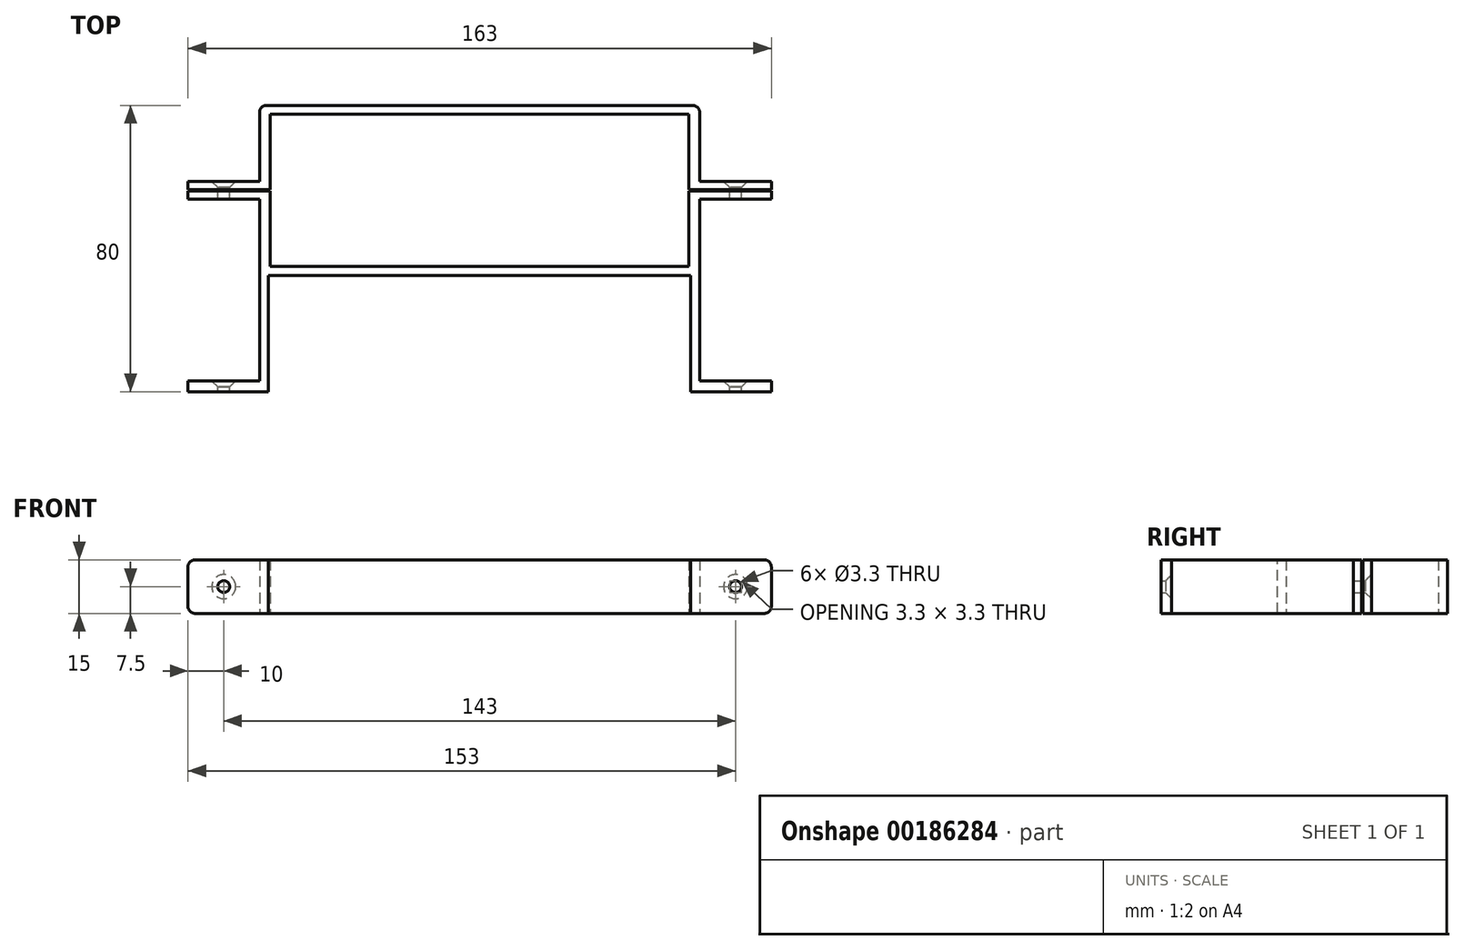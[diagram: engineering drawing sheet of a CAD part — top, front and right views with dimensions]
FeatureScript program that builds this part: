
annotation { "Feature Type Name" : "Feature", "Feature Type Description" : "" }
export const myFeature = defineFeature(function(context is Context, id is Id, definition is map)
    precondition{}
    {
        {
            var Q0;
            Q0=qCreatedBy(makeId("Top.planeOp"),FACE);
            var sketch = newSketch(context, id + "F0", { "sketchPlane" : qUnion([Q0])});
            skLineSegment(sketch, "E0.bottom", {"start": v(61.5, -23.75) * mm, "end": v(-61.5, -23.75) * mm});
            skLineSegment(sketch, "E0.top", {"start": v(61.5, 23.75) * mm, "end": v(-61.5, 23.75) * mm});
            skLineSegment(sketch, "E0.left", {"start": v(61.5, -23.75) * mm, "end": v(61.5, 23.75) * mm});
            skLineSegment(sketch, "E0.right", {"start": v(-61.5, -23.75) * mm, "end": v(-61.5, 23.75) * mm});
            skPoint(sketch, "E0.middle", {"position": v(0, 0) * mm});
            skLineSegment(sketch, "E1.bottom", {"start": v(58.5, -21.25) * mm, "end": v(-58.5, -21.25) * mm});
            skLineSegment(sketch, "E1.top", {"start": v(58.5, 21.25) * mm, "end": v(-58.5, 21.25) * mm});
            skLineSegment(sketch, "E1.left", {"start": v(58.5, -21.25) * mm, "end": v(58.5, 21.25) * mm});
            skLineSegment(sketch, "E1.right", {"start": v(-58.5, -21.25) * mm, "end": v(-58.5, 21.25) * mm});
            skSolve(sketch);
        }
        {
            var Q0;
            Q0=makeQuery(id+"F0.imprint","IMPRINT",FACE,{"disambiguationData":[TD([[makeQuery(id+"F0.imprint","IMPRINT",EDGE,{"derivedFrom":sQuery(id+"F0.wireOp",EDGE,"E0.bottom")}),-1.0]])]});
            extrude(context, id + "F1", {"entities" : qUnion([Q0]), "depth" : 15 * mm, "offsetDistance" : 25 * mm});
        }
        {
            var Q0;
            Q0=makeQuery(id+"F1.opExtrude","CAP_FACE",FACE,{"disambiguationData":[OSD([sQuery(id+"F0.wireOp",EDGE,"E0.bottom"),sQuery(id+"F0.wireOp",EDGE,"E0.top"),sQuery(id+"F0.wireOp",EDGE,"E0.left"),sQuery(id+"F0.wireOp",EDGE,"E0.right"),sQuery(id+"F0.wireOp",EDGE,"E1.bottom"),sQuery(id+"F0.wireOp",EDGE,"E1.top"),sQuery(id+"F0.wireOp",EDGE,"E1.left"),sQuery(id+"F0.wireOp",EDGE,"E1.right")])],"isStart":false});
            var sketch = newSketch(context, id + "F2", { "sketchPlane" : qUnion([Q0])});
            skLineSegment(sketch, "E2.bottom", {"start": v(-55, -25) * mm, "end": v(55, -25) * mm});
            skLineSegment(sketch, "E2.top", {"start": v(-55, 25) * mm, "end": v(55, 25) * mm});
            skLineSegment(sketch, "E2.left", {"start": v(-55, -25) * mm, "end": v(-55, 25) * mm});
            skLineSegment(sketch, "E2.right", {"start": v(55, -25) * mm, "end": v(55, 25) * mm});
            skPoint(sketch, "E2.middle", {"position": v(0, 0) * mm});
            skSolve(sketch);
        }
        {
            var Q0;
            Q0=makeQuery(id+"F1.opExtrude","SWEPT_FACE",FACE,{"disambiguationData":[OSD([sQuery(id+"F0.wireOp",EDGE,"E0.bottom")])]});
            var sketch = newSketch(context, id + "F3", { "sketchPlane" : qUnion([Q0])});
            skPoint(sketch, "E3", {"position": v(-59, 15) * mm});
            skPoint(sketch, "E4", {"position": v(-59, 0) * mm});
            skPoint(sketch, "E5", {"position": v(59, 15) * mm});
            skPoint(sketch, "E6", {"position": v(59, 0) * mm});
            skLineSegment(sketch, "E7", {"start": v(-59, 15) * mm, "end": v(-59, 0) * mm});
            skLineSegment(sketch, "E8", {"start": v(59, 0) * mm, "end": v(59, 15) * mm});
            skSolve(sketch);
        }
        {
            var Q0;
            {var subQ0=sQuery(id+"F3.wireOp",EDGE,"E7");Q0=makeQuery(id+"F3.imprint","IMPRINT",FACE,{"disambiguationData":[TD([[makeQuery(id+"F3.imprint","IMPRINT",EDGE,{"derivedFrom":subQ0}),-1.0]])]});}
            var Q1;
            {var subQ0=sQuery(id+"F3.wireOp",EDGE,"E8");Q1=makeQuery(id+"F3.imprint","IMPRINT",FACE,{"disambiguationData":[TD([[makeQuery(id+"F3.imprint","IMPRINT",EDGE,{"derivedFrom":subQ0}),-1.0]])]});}
            extrude(context, id + "F4", {"entities" : qUnion([Q0, Q1]), "operationType" : NewBodyOperationType.ADD, "depth" : 32.5 * mm, "offsetDistance" : 25 * mm});
        }
        {
            var Q0;
            {var subQ0=sQuery(id+"F0.wireOp",EDGE,"E0.right");Q0=makeQuery(id+"F4.boolean.opBoolean","MERGE",FACE,{"derivedFrom":[makeQuery(id+"F1.opExtrude","SWEPT_FACE",FACE,{"disambiguationData":[OSD([subQ0])]}),makeQuery(id+"F4.opExtrude","SWEPT_FACE",FACE,{"disambiguationData":[OSD([sQuery(id+"F0.wireOp",EDGE,"E0.bottom"),subQ0])]})]});}
            var sketch = newSketch(context, id + "F5", { "sketchPlane" : qUnion([Q0])});
            skPoint(sketch, "E9", {"position": v(53.25, 15) * mm});
            skPoint(sketch, "E10", {"position": v(53.25, 0) * mm});
            skLineSegment(sketch, "E11", {"start": v(53.25, 15) * mm, "end": v(53.25, 0) * mm});
            skSolve(sketch);
        }
        {
            var Q0;
            {var subQ0=sQuery(id+"F5.wireOp",EDGE,"E11");Q0=makeQuery(id+"F5.imprint","IMPRINT",FACE,{"disambiguationData":[TD([[makeQuery(id+"F5.imprint","IMPRINT",EDGE,{"derivedFrom":subQ0}),1.0]])]});}
            extrude(context, id + "F6", {"entities" : qUnion([Q0]), "operationType" : NewBodyOperationType.ADD, "depth" : 20 * mm, "offsetDistance" : 25 * mm});
        }
        {
            var Q0;
            {var subQ0=sQuery(id+"F0.wireOp",EDGE,"E0.left");Q0=makeQuery(id+"F4.boolean.opBoolean","MERGE",FACE,{"derivedFrom":[makeQuery(id+"F1.opExtrude","SWEPT_FACE",FACE,{"disambiguationData":[OSD([subQ0])]}),makeQuery(id+"F4.opExtrude","SWEPT_FACE",FACE,{"disambiguationData":[OSD([sQuery(id+"F0.wireOp",EDGE,"E0.bottom"),subQ0])]})]});}
            var sketch = newSketch(context, id + "F7", { "sketchPlane" : qUnion([Q0])});
            skPoint(sketch, "E12", {"position": v(-53.25, 15) * mm});
            skPoint(sketch, "E13", {"position": v(-53.25, 0) * mm});
            skLineSegment(sketch, "E14", {"start": v(-53.25, 15) * mm, "end": v(-53.25, 0) * mm});
            skSolve(sketch);
        }
        {
            var Q0;
            {var subQ0=sQuery(id+"F7.wireOp",EDGE,"E14");Q0=makeQuery(id+"F7.imprint","IMPRINT",FACE,{"disambiguationData":[TD([[makeQuery(id+"F7.imprint","IMPRINT",EDGE,{"derivedFrom":subQ0}),-1.0]])]});}
            extrude(context, id + "F8", {"entities" : qUnion([Q0]), "operationType" : NewBodyOperationType.ADD, "depth" : 20 * mm, "offsetDistance" : 25 * mm});
        }
        {
            var Q0;
            Q0=makeQuery(id+"F8.opExtrude","SWEPT_FACE",FACE,{"disambiguationData":[OSD([sQuery(id+"F7.wireOp",EDGE,"E14")])]});
            var sketch = newSketch(context, id + "F9", { "sketchPlane" : qUnion([Q0])});
            skPoint(sketch, "E15", {"position": v(-71.5, 7.5) * mm});
            skPoint(sketch, "E15.positionSnap0", {"position": v(-71.5, 0) * mm});
            skPoint(sketch, "E15.positionSnap1", {"position": v(-61.5, 7.5) * mm});
            skSolve(sketch);
        }
        {
            var Q0;
            Q0=sQuery(id+"F9.wireOp",VERTEX,"E15");
            var Q1;
            Q1=makeQuery(id+"F1.opExtrude","SWEPT_BODY",BODY,{"disambiguationData":[OSD([sQuery(id+"F0.wireOp",EDGE,"E0.bottom"),sQuery(id+"F0.wireOp",EDGE,"E0.top"),sQuery(id+"F0.wireOp",EDGE,"E0.left"),sQuery(id+"F0.wireOp",EDGE,"E0.right"),sQuery(id+"F0.wireOp",EDGE,"E1.bottom"),sQuery(id+"F0.wireOp",EDGE,"E1.top"),sQuery(id+"F0.wireOp",EDGE,"E1.left"),sQuery(id+"F0.wireOp",EDGE,"E1.right")])]});
            hole(context, id + "F10", {"style" : HoleStyle.C_SINK, "endStyle" : HoleEndStyle.BLIND, "standardTappedOrClearance" : lookupTablePath({ "standard" : "ISO", "fit" : "Normal", "size" : "M3", "type" : "Clearance" }), "standardBlindInLast" : lookupTablePath({ "fit" : "Standard", "standard" : "ISO", "size" : "M3", "type" : "Clearance" }), "holeDiameter" : 3.3 * mm, "cSinkDiameter" : 6.72 * mm, "cSinkAngle" : 90 * degree, "majorDiameter" : 5 * mm, "holeDepth" : 5 * mm, "isTappedThrough" : true, "tappedDepth" : 12 * mm, "tapClearance" : 3, "startFromSketch" : true, "locations" : qUnion([Q0]), "scope" : qUnion([Q1])});
        }
        {
            var Q0;
            Q0=makeQuery(id+"F6.opExtrude","SWEPT_FACE",FACE,{"disambiguationData":[OSD([sQuery(id+"F5.wireOp",EDGE,"E11")])]});
            var sketch = newSketch(context, id + "F11", { "sketchPlane" : qUnion([Q0])});
            skPoint(sketch, "E16", {"position": v(71.5, 7.5) * mm});
            skPoint(sketch, "E16.positionSnap0", {"position": v(81.5, 7.5) * mm});
            skPoint(sketch, "E16.positionSnap1", {"position": v(71.5, 0) * mm});
            skSolve(sketch);
        }
        {
            var Q0;
            Q0=sQuery(id+"F11.wireOp",VERTEX,"E16");
            var Q1;
            Q1=makeQuery(id+"F1.opExtrude","SWEPT_BODY",BODY,{"disambiguationData":[OSD([sQuery(id+"F0.wireOp",EDGE,"E0.bottom"),sQuery(id+"F0.wireOp",EDGE,"E0.top"),sQuery(id+"F0.wireOp",EDGE,"E0.left"),sQuery(id+"F0.wireOp",EDGE,"E0.right"),sQuery(id+"F0.wireOp",EDGE,"E1.bottom"),sQuery(id+"F0.wireOp",EDGE,"E1.top"),sQuery(id+"F0.wireOp",EDGE,"E1.left"),sQuery(id+"F0.wireOp",EDGE,"E1.right")])]});
            hole(context, id + "F12", {"style" : HoleStyle.C_SINK, "endStyle" : HoleEndStyle.BLIND, "standardTappedOrClearance" : lookupTablePath({ "standard" : "ISO", "fit" : "Normal", "size" : "M3", "type" : "Clearance" }), "standardBlindInLast" : lookupTablePath({ "fit" : "Standard", "standard" : "ISO", "size" : "M3", "type" : "Clearance" }), "holeDiameter" : 3.3 * mm, "cSinkDiameter" : 6.72 * mm, "cSinkAngle" : 90 * degree, "majorDiameter" : 5 * mm, "holeDepth" : 5 * mm, "isTappedThrough" : true, "tappedDepth" : 12 * mm, "tapClearance" : 3, "startFromSketch" : true, "locations" : qUnion([Q0]), "scope" : qUnion([Q1])});
        }
        {
            var Q0;
            {var subQ0=sQuery(id+"F0.wireOp",EDGE,"E0.right");Q0=makeQuery(id+"F4.boolean.opBoolean","MERGE",FACE,{"derivedFrom":[makeQuery(id+"F1.opExtrude","SWEPT_FACE",FACE,{"disambiguationData":[OSD([subQ0])]}),makeQuery(id+"F4.opExtrude","SWEPT_FACE",FACE,{"disambiguationData":[OSD([sQuery(id+"F0.wireOp",EDGE,"E0.bottom"),subQ0])]})]});}
            var sketch = newSketch(context, id + "F13", { "sketchPlane" : qUnion([Q0])});
            skPoint(sketch, "E17", {"position": v(-2.5, 0) * mm});
            skPoint(sketch, "E18", {"position": v(2.5, 0) * mm});
            skPoint(sketch, "E19", {"position": v(2.5, 15) * mm});
            skPoint(sketch, "E20", {"position": v(-2.5, 15) * mm});
            skPoint(sketch, "E21", {"position": v(0, 0) * mm});
            skPoint(sketch, "E22", {"position": v(0, 15) * mm});
            skLineSegment(sketch, "E23", {"start": v(-2.5, 0) * mm, "end": v(-2.5, 15) * mm});
            skLineSegment(sketch, "E24", {"start": v(2.5, 15) * mm, "end": v(2.5, 0) * mm});
            skSolve(sketch);
        }
        {
            var Q0;
            {var subQ0=sQuery(id+"F13.wireOp",EDGE,"E23");Q0=makeQuery(id+"F13.imprint","IMPRINT",FACE,{"disambiguationData":[TD([[makeQuery(id+"F13.imprint","IMPRINT",EDGE,{"derivedFrom":subQ0}),-1.0]])]});}
            extrude(context, id + "F14", {"entities" : qUnion([Q0]), "operationType" : NewBodyOperationType.ADD, "depth" : 20 * mm, "offsetDistance" : 25 * mm});
        }
        {
            var Q0;
            Q0=makeQuery(id+"F14.opExtrude","SWEPT_FACE",FACE,{"disambiguationData":[OSD([sQuery(id+"F13.wireOp",EDGE,"E23")])]});
            var sketch = newSketch(context, id + "F15", { "sketchPlane" : qUnion([Q0])});
            skPoint(sketch, "E25", {"position": v(71.5, 7.5) * mm});
            skPoint(sketch, "E25.positionSnap0", {"position": v(71.5, 0) * mm});
            skPoint(sketch, "E25.positionSnap1", {"position": v(81.5, 7.5) * mm});
            skSolve(sketch);
        }
        {
            var Q0;
            Q0=sQuery(id+"F15.wireOp",VERTEX,"E25");
            var Q1;
            Q1=makeQuery(id+"F1.opExtrude","SWEPT_BODY",BODY,{"disambiguationData":[OSD([sQuery(id+"F0.wireOp",EDGE,"E0.bottom"),sQuery(id+"F0.wireOp",EDGE,"E0.top"),sQuery(id+"F0.wireOp",EDGE,"E0.left"),sQuery(id+"F0.wireOp",EDGE,"E0.right"),sQuery(id+"F0.wireOp",EDGE,"E1.bottom"),sQuery(id+"F0.wireOp",EDGE,"E1.top"),sQuery(id+"F0.wireOp",EDGE,"E1.left"),sQuery(id+"F0.wireOp",EDGE,"E1.right")])]});
            hole(context, id + "F16", {"style" : HoleStyle.C_SINK, "endStyle" : HoleEndStyle.THROUGH, "standardTappedOrClearance" : lookupTablePath({ "standard" : "ISO", "fit" : "Normal", "size" : "M3", "type" : "Clearance" }), "standardBlindInLast" : lookupTablePath({ "fit" : "Standard", "standard" : "ISO", "size" : "M3", "type" : "Clearance" }), "holeDiameter" : 3.3 * mm, "cSinkDiameter" : 6.72 * mm, "cSinkAngle" : 90 * degree, "majorDiameter" : 5 * mm, "isTappedThrough" : true, "tappedDepth" : 12 * mm, "tapClearance" : 3, "startFromSketch" : true, "locations" : qUnion([Q0]), "scope" : qUnion([Q1])});
        }
        {
            var Q0;
            {var subQ0=sQuery(id+"F0.wireOp",EDGE,"E0.left");Q0=makeQuery(id+"F4.boolean.opBoolean","MERGE",FACE,{"derivedFrom":[makeQuery(id+"F1.opExtrude","SWEPT_FACE",FACE,{"disambiguationData":[OSD([subQ0])]}),makeQuery(id+"F4.opExtrude","SWEPT_FACE",FACE,{"disambiguationData":[OSD([sQuery(id+"F0.wireOp",EDGE,"E0.bottom"),subQ0])]})]});}
            var sketch = newSketch(context, id + "F17", { "sketchPlane" : qUnion([Q0])});
            skPoint(sketch, "E26", {"position": v(0, 0) * mm});
            skPoint(sketch, "E27", {"position": v(0, 15) * mm});
            skPoint(sketch, "E28", {"position": v(2.5, 15) * mm});
            skPoint(sketch, "E29", {"position": v(2.5, 0) * mm});
            skPoint(sketch, "E30", {"position": v(-2.5, 0) * mm});
            skPoint(sketch, "E31", {"position": v(-2.5, 15) * mm});
            skLineSegment(sketch, "E32", {"start": v(-2.5, 15) * mm, "end": v(-2.5, 0) * mm});
            skLineSegment(sketch, "E33", {"start": v(2.5, 0) * mm, "end": v(2.5, 15) * mm});
            skSolve(sketch);
        }
        {
            var Q0;
            {var subQ0=sQuery(id+"F17.wireOp",EDGE,"E32");Q0=makeQuery(id+"F17.imprint","IMPRINT",FACE,{"disambiguationData":[TD([[makeQuery(id+"F17.imprint","IMPRINT",EDGE,{"derivedFrom":subQ0}),1.0]])]});}
            extrude(context, id + "F18", {"entities" : qUnion([Q0]), "operationType" : NewBodyOperationType.ADD, "depth" : 20 * mm, "offsetDistance" : 25 * mm});
        }
        {
            var Q0;
            Q0=makeQuery(id+"F18.opExtrude","SWEPT_FACE",FACE,{"disambiguationData":[OSD([sQuery(id+"F17.wireOp",EDGE,"E33")])]});
            var sketch = newSketch(context, id + "F19", { "sketchPlane" : qUnion([Q0])});
            skPoint(sketch, "E34", {"position": v(-71.5, 7.5) * mm});
            skPoint(sketch, "E34.positionSnap0", {"position": v(-71.5, 15) * mm});
            skPoint(sketch, "E34.positionSnap1", {"position": v(-81.5, 7.5) * mm});
            skSolve(sketch);
        }
        {
            var Q0;
            Q0=sQuery(id+"F19.wireOp",VERTEX,"E34");
            var Q1;
            Q1=makeQuery(id+"F1.opExtrude","SWEPT_BODY",BODY,{"disambiguationData":[OSD([sQuery(id+"F0.wireOp",EDGE,"E0.bottom"),sQuery(id+"F0.wireOp",EDGE,"E0.top"),sQuery(id+"F0.wireOp",EDGE,"E0.left"),sQuery(id+"F0.wireOp",EDGE,"E0.right"),sQuery(id+"F0.wireOp",EDGE,"E1.bottom"),sQuery(id+"F0.wireOp",EDGE,"E1.top"),sQuery(id+"F0.wireOp",EDGE,"E1.left"),sQuery(id+"F0.wireOp",EDGE,"E1.right")])]});
            hole(context, id + "F20", {"style" : HoleStyle.C_SINK, "endStyle" : HoleEndStyle.THROUGH, "standardTappedOrClearance" : lookupTablePath({ "standard" : "ISO", "fit" : "Normal", "size" : "M3", "type" : "Clearance" }), "standardBlindInLast" : lookupTablePath({ "fit" : "Standard", "standard" : "ISO", "size" : "M3", "type" : "Clearance" }), "holeDiameter" : 3.3 * mm, "cSinkDiameter" : 6.72 * mm, "cSinkAngle" : 90 * degree, "majorDiameter" : 5 * mm, "isTappedThrough" : true, "tappedDepth" : 12 * mm, "tapClearance" : 3, "startFromSketch" : true, "locations" : qUnion([Q0]), "scope" : qUnion([Q1])});
        }
        {
            var Q0;
            Q0=makeQuery(id+"F18.opExtrude","CAP_FACE",FACE,{"disambiguationData":[OSD([sQuery(id+"F0.wireOp",EDGE,"E0.bottom"),sQuery(id+"F0.wireOp",EDGE,"E0.left"),sQuery(id+"F17.wireOp",EDGE,"E32"),sQuery(id+"F17.wireOp",EDGE,"E33")])],"isStart":false});
            var sketch = newSketch(context, id + "F21", { "sketchPlane" : qUnion([Q0])});
            skPoint(sketch, "E35", {"position": v(0, 0) * mm});
            skPoint(sketch, "E36", {"position": v(0, 15) * mm});
            skPoint(sketch, "E37", {"position": v(0.2, 15) * mm});
            skPoint(sketch, "E38", {"position": v(-0.2, 15) * mm});
            skPoint(sketch, "E39", {"position": v(-0.2, 0) * mm});
            skPoint(sketch, "E40", {"position": v(0.2, 0) * mm});
            skLineSegment(sketch, "E41", {"start": v(-0.2, 15) * mm, "end": v(-0.2, 0) * mm});
            skLineSegment(sketch, "E42", {"start": v(0.2, 0) * mm, "end": v(0.2, 15) * mm});
            skSolve(sketch);
        }
        {
            var Q0;
            {var subQ0=sQuery(id+"F21.wireOp",EDGE,"E41");Q0=makeQuery(id+"F21.imprint","IMPRINT",FACE,{"disambiguationData":[TD([[makeQuery(id+"F21.imprint","IMPRINT",EDGE,{"derivedFrom":subQ0}),1.0]])]});}
            extrude(context, id + "F22", {"entities" : qUnion([Q0]), "operationType" : NewBodyOperationType.REMOVE, "oppositeDirection" : true, "depth" : 200 * mm, "offsetDistance" : 25 * mm});
        }
        {
            var Q0;
            Q0=makeQuery(id+"F1.opExtrude","SWEPT_EDGE",EDGE,{"disambiguationData":[OSD([sQuery(id+"F0.wireOp",EDGE,"E0.top"),sQuery(id+"F0.wireOp",EDGE,"E0.right")])]});
            var Q1;
            {var subQ0=sQuery(id+"F0.wireOp",EDGE,"E0.bottom");var subQ1=sQuery(id+"F0.wireOp",EDGE,"E0.right");var subQ2=makeQuery(id+"F4.boolean.opBoolean","MERGE",EDGE,{"derivedFrom":[makeQuery(id+"F1.opExtrude","CAP_EDGE",EDGE,{"disambiguationData":[OSD([subQ1])],"isStart":true}),makeQuery(id+"F4.opExtrude","SWEPT_EDGE",EDGE,{"disambiguationData":[OSD([subQ0,subQ1]),TDD([makeQuery(id+"F3.imprint","INTERSECT",VERTEX,{"derivedFrom":[makeQuery(id+"F1.opExtrude","SWEPT_EDGE",EDGE,{"disambiguationData":[OSD([subQ0,subQ1])]}),makeQuery(id+"F1.opExtrude","CAP_EDGE",EDGE,{"disambiguationData":[OSD([subQ0])],"isStart":true})]})])]})]});Q1=makeQuery(id+"F6.opExtrude","CAP_EDGE",EDGE,{"disambiguationData":[OSD([subQ0,subQ1]),TDD([makeQuery(id+"F5.imprint","IMPRINT",EDGE,{"disambiguationData":[TD([[makeQuery(id+"F5.imprint","INTERSECT",VERTEX,{"derivedFrom":[subQ2,sQuery(id+"F5.wireOp",EDGE,"E11")]}),1.0]])],"derivedFrom":subQ2})])],"isStart":false});}
            var Q2;
            {var subQ0=sQuery(id+"F0.wireOp",EDGE,"E0.bottom");var subQ1=sQuery(id+"F0.wireOp",EDGE,"E0.right");var subQ2=makeQuery(id+"F4.boolean.opBoolean","MERGE",EDGE,{"derivedFrom":[makeQuery(id+"F1.opExtrude","CAP_EDGE",EDGE,{"disambiguationData":[OSD([subQ1])],"isStart":false}),makeQuery(id+"F4.opExtrude","SWEPT_EDGE",EDGE,{"disambiguationData":[OSD([subQ0,subQ1]),TDD([makeQuery(id+"F3.imprint","INTERSECT",VERTEX,{"derivedFrom":[makeQuery(id+"F1.opExtrude","SWEPT_EDGE",EDGE,{"disambiguationData":[OSD([subQ0,subQ1])]}),makeQuery(id+"F1.opExtrude","CAP_EDGE",EDGE,{"disambiguationData":[OSD([subQ0])],"isStart":false})]})])]})]});Q2=makeQuery(id+"F6.opExtrude","CAP_EDGE",EDGE,{"disambiguationData":[OSD([subQ0,subQ1]),TDD([makeQuery(id+"F5.imprint","IMPRINT",EDGE,{"disambiguationData":[TD([[makeQuery(id+"F5.imprint","INTERSECT",VERTEX,{"derivedFrom":[subQ2,sQuery(id+"F5.wireOp",EDGE,"E11")]}),1.0]])],"derivedFrom":subQ2})])],"isStart":false});}
            var Q3;
            {var subQ0=sQuery(id+"F0.wireOp",EDGE,"E0.bottom");var subQ1=sQuery(id+"F0.wireOp",EDGE,"E0.left");var subQ2=makeQuery(id+"F4.boolean.opBoolean","MERGE",EDGE,{"derivedFrom":[makeQuery(id+"F1.opExtrude","CAP_EDGE",EDGE,{"disambiguationData":[OSD([subQ1])],"isStart":true}),makeQuery(id+"F4.opExtrude","SWEPT_EDGE",EDGE,{"disambiguationData":[OSD([subQ0,subQ1]),TDD([makeQuery(id+"F3.imprint","INTERSECT",VERTEX,{"derivedFrom":[makeQuery(id+"F1.opExtrude","SWEPT_EDGE",EDGE,{"disambiguationData":[OSD([subQ0,subQ1])]}),makeQuery(id+"F1.opExtrude","CAP_EDGE",EDGE,{"disambiguationData":[OSD([subQ0])],"isStart":true})]})])]})]});Q3=makeQuery(id+"F8.opExtrude","CAP_EDGE",EDGE,{"disambiguationData":[OSD([subQ0,subQ1]),TDD([makeQuery(id+"F7.imprint","IMPRINT",EDGE,{"disambiguationData":[TD([[makeQuery(id+"F7.imprint","INTERSECT",VERTEX,{"derivedFrom":[subQ2,sQuery(id+"F7.wireOp",EDGE,"E14")]}),1.0]])],"derivedFrom":subQ2})])],"isStart":false});}
            var Q4;
            {var subQ0=sQuery(id+"F0.wireOp",EDGE,"E0.bottom");var subQ1=sQuery(id+"F0.wireOp",EDGE,"E0.left");var subQ2=makeQuery(id+"F4.boolean.opBoolean","MERGE",EDGE,{"derivedFrom":[makeQuery(id+"F1.opExtrude","CAP_EDGE",EDGE,{"disambiguationData":[OSD([subQ1])],"isStart":false}),makeQuery(id+"F4.opExtrude","SWEPT_EDGE",EDGE,{"disambiguationData":[OSD([subQ0,subQ1]),TDD([makeQuery(id+"F3.imprint","INTERSECT",VERTEX,{"derivedFrom":[makeQuery(id+"F1.opExtrude","SWEPT_EDGE",EDGE,{"disambiguationData":[OSD([subQ0,subQ1])]}),makeQuery(id+"F1.opExtrude","CAP_EDGE",EDGE,{"disambiguationData":[OSD([subQ0])],"isStart":false})]})])]})]});Q4=makeQuery(id+"F8.opExtrude","CAP_EDGE",EDGE,{"disambiguationData":[OSD([subQ0,subQ1]),TDD([makeQuery(id+"F7.imprint","IMPRINT",EDGE,{"disambiguationData":[TD([[makeQuery(id+"F7.imprint","INTERSECT",VERTEX,{"derivedFrom":[subQ2,sQuery(id+"F7.wireOp",EDGE,"E14")]}),1.0]])],"derivedFrom":subQ2})])],"isStart":false});}
            var Q5;
            Q5=makeQuery(id+"F1.opExtrude","SWEPT_EDGE",EDGE,{"disambiguationData":[OSD([sQuery(id+"F0.wireOp",EDGE,"E0.top"),sQuery(id+"F0.wireOp",EDGE,"E0.left")])]});
            var Q6;
            Q6=makeQuery(id+"F6.opExtrude","CAP_EDGE",EDGE,{"disambiguationData":[OSD([sQuery(id+"F5.wireOp",EDGE,"E11")])],"isStart":true});
            var Q7;
            Q7=makeQuery(id+"F8.opExtrude","CAP_EDGE",EDGE,{"disambiguationData":[OSD([sQuery(id+"F7.wireOp",EDGE,"E14")])],"isStart":true});
            var Q8;
            {var subQ2=sQuery(id+"F0.wireOp",EDGE,"E0.bottom");var subQ3=makeQuery(id+"F1.opExtrude","CAP_EDGE",EDGE,{"disambiguationData":[OSD([subQ2])],"isStart":true});var subQ10=sQuery(id+"F0.wireOp",EDGE,"E0.left");var subQ11=makeQuery(id+"F3.imprint","INTERSECT",VERTEX,{"derivedFrom":[makeQuery(id+"F1.opExtrude","SWEPT_EDGE",EDGE,{"disambiguationData":[OSD([subQ2,subQ10])]}),subQ3]});var subQ12=makeQuery(id+"F4.boolean.opBoolean","MERGE",EDGE,{"derivedFrom":[makeQuery(id+"F1.opExtrude","CAP_EDGE",EDGE,{"disambiguationData":[OSD([subQ10])],"isStart":true}),makeQuery(id+"F4.opExtrude","SWEPT_EDGE",EDGE,{"disambiguationData":[OSD([subQ2,subQ10]),TDD([subQ11])]})]});var subQ13=sQuery(id+"F17.wireOp",EDGE,"E32");var subQ15=subQ12;var subQ16=makeQuery(id+"F17.imprint","IMPRINT",EDGE,{"disambiguationData":[TD([[makeQuery(id+"F17.imprint","INTERSECT",VERTEX,{"derivedFrom":[subQ15,subQ13]}),-1.0]])],"derivedFrom":subQ15});Q8=makeQuery(id+"F22.boolean.opBoolean","SPLIT",EDGE,{"disambiguationData":[TD([makeQuery(id+"F18.opExtrude","SWEPT_FACE",FACE,{"disambiguationData":[OSD([subQ13])]})])],"derivedFrom":makeQuery(id+"F18.opExtrude","CAP_EDGE",EDGE,{"disambiguationData":[OSD([subQ2,subQ10]),TDD([subQ16])],"isStart":false})});}
            var Q9;
            {var subQ2=sQuery(id+"F0.wireOp",EDGE,"E0.bottom");var subQ3=makeQuery(id+"F1.opExtrude","CAP_EDGE",EDGE,{"disambiguationData":[OSD([subQ2])],"isStart":true});var subQ10=sQuery(id+"F17.wireOp",EDGE,"E33");var subQ11=sQuery(id+"F0.wireOp",EDGE,"E0.left");var subQ12=makeQuery(id+"F3.imprint","INTERSECT",VERTEX,{"derivedFrom":[makeQuery(id+"F1.opExtrude","SWEPT_EDGE",EDGE,{"disambiguationData":[OSD([subQ2,subQ11])]}),subQ3]});var subQ13=makeQuery(id+"F4.boolean.opBoolean","MERGE",EDGE,{"derivedFrom":[makeQuery(id+"F1.opExtrude","CAP_EDGE",EDGE,{"disambiguationData":[OSD([subQ11])],"isStart":true}),makeQuery(id+"F4.opExtrude","SWEPT_EDGE",EDGE,{"disambiguationData":[OSD([subQ2,subQ11]),TDD([subQ12])]})]});var subQ14=sQuery(id+"F17.wireOp",EDGE,"E32");var subQ15=subQ13;var subQ16=makeQuery(id+"F17.imprint","IMPRINT",EDGE,{"disambiguationData":[TD([[makeQuery(id+"F17.imprint","INTERSECT",VERTEX,{"derivedFrom":[subQ15,subQ14]}),-1.0]])],"derivedFrom":subQ15});Q9=makeQuery(id+"F22.boolean.opBoolean","SPLIT",EDGE,{"disambiguationData":[TD([makeQuery(id+"F18.opExtrude","SWEPT_FACE",FACE,{"disambiguationData":[OSD([subQ10])]})])],"derivedFrom":makeQuery(id+"F18.opExtrude","CAP_EDGE",EDGE,{"disambiguationData":[OSD([subQ2,subQ11]),TDD([subQ16])],"isStart":false})});}
            var Q10;
            {var subQ0=sQuery(id+"F0.wireOp",EDGE,"E0.bottom");var subQ1=makeQuery(id+"F1.opExtrude","CAP_EDGE",EDGE,{"disambiguationData":[OSD([subQ0])],"isStart":false});var subQ5=sQuery(id+"F0.wireOp",EDGE,"E0.left");var subQ6=makeQuery(id+"F3.imprint","INTERSECT",VERTEX,{"derivedFrom":[makeQuery(id+"F1.opExtrude","SWEPT_EDGE",EDGE,{"disambiguationData":[OSD([subQ0,subQ5])]}),subQ1]});var subQ7=makeQuery(id+"F4.boolean.opBoolean","MERGE",EDGE,{"derivedFrom":[makeQuery(id+"F1.opExtrude","CAP_EDGE",EDGE,{"disambiguationData":[OSD([subQ5])],"isStart":false}),makeQuery(id+"F4.opExtrude","SWEPT_EDGE",EDGE,{"disambiguationData":[OSD([subQ0,subQ5]),TDD([subQ6])]})]});var subQ9=sQuery(id+"F17.wireOp",EDGE,"E32");var subQ11=subQ7;var subQ12=makeQuery(id+"F17.imprint","IMPRINT",EDGE,{"disambiguationData":[TD([[makeQuery(id+"F17.imprint","INTERSECT",VERTEX,{"derivedFrom":[subQ11,subQ9]}),-1.0]])],"derivedFrom":subQ11});Q10=makeQuery(id+"F22.boolean.opBoolean","SPLIT",EDGE,{"disambiguationData":[TD([makeQuery(id+"F18.opExtrude","SWEPT_FACE",FACE,{"disambiguationData":[OSD([subQ9])]})])],"derivedFrom":makeQuery(id+"F18.opExtrude","CAP_EDGE",EDGE,{"disambiguationData":[OSD([subQ0,subQ5]),TDD([subQ12])],"isStart":false})});}
            var Q11;
            {var subQ0=sQuery(id+"F0.wireOp",EDGE,"E0.bottom");var subQ1=makeQuery(id+"F1.opExtrude","CAP_EDGE",EDGE,{"disambiguationData":[OSD([subQ0])],"isStart":false});var subQ5=sQuery(id+"F0.wireOp",EDGE,"E0.left");var subQ6=makeQuery(id+"F3.imprint","INTERSECT",VERTEX,{"derivedFrom":[makeQuery(id+"F1.opExtrude","SWEPT_EDGE",EDGE,{"disambiguationData":[OSD([subQ0,subQ5])]}),subQ1]});var subQ7=makeQuery(id+"F4.boolean.opBoolean","MERGE",EDGE,{"derivedFrom":[makeQuery(id+"F1.opExtrude","CAP_EDGE",EDGE,{"disambiguationData":[OSD([subQ5])],"isStart":false}),makeQuery(id+"F4.opExtrude","SWEPT_EDGE",EDGE,{"disambiguationData":[OSD([subQ0,subQ5]),TDD([subQ6])]})]});var subQ9=sQuery(id+"F17.wireOp",EDGE,"E33");var subQ10=sQuery(id+"F17.wireOp",EDGE,"E32");var subQ11=subQ7;var subQ12=makeQuery(id+"F17.imprint","IMPRINT",EDGE,{"disambiguationData":[TD([[makeQuery(id+"F17.imprint","INTERSECT",VERTEX,{"derivedFrom":[subQ11,subQ10]}),-1.0]])],"derivedFrom":subQ11});Q11=makeQuery(id+"F22.boolean.opBoolean","SPLIT",EDGE,{"disambiguationData":[TD([makeQuery(id+"F18.opExtrude","SWEPT_FACE",FACE,{"disambiguationData":[OSD([subQ9])]})])],"derivedFrom":makeQuery(id+"F18.opExtrude","CAP_EDGE",EDGE,{"disambiguationData":[OSD([subQ0,subQ5]),TDD([subQ12])],"isStart":false})});}
            var Q12;
            {var subQ0=sQuery(id+"F0.wireOp",EDGE,"E0.bottom");var subQ1=makeQuery(id+"F1.opExtrude","CAP_EDGE",EDGE,{"disambiguationData":[OSD([subQ0])],"isStart":false});var subQ2=sQuery(id+"F0.wireOp",EDGE,"E0.right");var subQ3=makeQuery(id+"F3.imprint","INTERSECT",VERTEX,{"derivedFrom":[makeQuery(id+"F1.opExtrude","SWEPT_EDGE",EDGE,{"disambiguationData":[OSD([subQ0,subQ2])]}),subQ1]});var subQ4=makeQuery(id+"F4.boolean.opBoolean","MERGE",EDGE,{"derivedFrom":[makeQuery(id+"F1.opExtrude","CAP_EDGE",EDGE,{"disambiguationData":[OSD([subQ2])],"isStart":false}),makeQuery(id+"F4.opExtrude","SWEPT_EDGE",EDGE,{"disambiguationData":[OSD([subQ0,subQ2]),TDD([subQ3])]})]});var subQ8=sQuery(id+"F13.wireOp",EDGE,"E23");var subQ9=subQ4;var subQ10=sQuery(id+"F13.wireOp",EDGE,"E24");var subQ11=makeQuery(id+"F13.imprint","IMPRINT",EDGE,{"disambiguationData":[TD([[makeQuery(id+"F13.imprint","INTERSECT",VERTEX,{"derivedFrom":[subQ9,subQ8]}),1.0]])],"derivedFrom":subQ9});Q12=makeQuery(id+"F22.boolean.opBoolean","SPLIT",EDGE,{"disambiguationData":[TD([makeQuery(id+"F14.opExtrude","SWEPT_FACE",FACE,{"disambiguationData":[OSD([subQ10])]})])],"derivedFrom":makeQuery(id+"F14.opExtrude","CAP_EDGE",EDGE,{"disambiguationData":[OSD([subQ0,subQ2]),TDD([subQ11])],"isStart":false})});}
            var Q13;
            {var subQ0=sQuery(id+"F0.wireOp",EDGE,"E0.bottom");var subQ1=makeQuery(id+"F1.opExtrude","CAP_EDGE",EDGE,{"disambiguationData":[OSD([subQ0])],"isStart":false});var subQ2=sQuery(id+"F0.wireOp",EDGE,"E0.right");var subQ3=makeQuery(id+"F3.imprint","INTERSECT",VERTEX,{"derivedFrom":[makeQuery(id+"F1.opExtrude","SWEPT_EDGE",EDGE,{"disambiguationData":[OSD([subQ0,subQ2])]}),subQ1]});var subQ4=makeQuery(id+"F4.boolean.opBoolean","MERGE",EDGE,{"derivedFrom":[makeQuery(id+"F1.opExtrude","CAP_EDGE",EDGE,{"disambiguationData":[OSD([subQ2])],"isStart":false}),makeQuery(id+"F4.opExtrude","SWEPT_EDGE",EDGE,{"disambiguationData":[OSD([subQ0,subQ2]),TDD([subQ3])]})]});var subQ7=sQuery(id+"F13.wireOp",EDGE,"E23");var subQ9=subQ4;var subQ11=makeQuery(id+"F13.imprint","IMPRINT",EDGE,{"disambiguationData":[TD([[makeQuery(id+"F13.imprint","INTERSECT",VERTEX,{"derivedFrom":[subQ9,subQ7]}),1.0]])],"derivedFrom":subQ9});Q13=makeQuery(id+"F22.boolean.opBoolean","SPLIT",EDGE,{"disambiguationData":[TD([makeQuery(id+"F14.opExtrude","SWEPT_FACE",FACE,{"disambiguationData":[OSD([subQ7])]})])],"derivedFrom":makeQuery(id+"F14.opExtrude","CAP_EDGE",EDGE,{"disambiguationData":[OSD([subQ0,subQ2]),TDD([subQ11])],"isStart":false})});}
            var Q14;
            {var subQ2=sQuery(id+"F13.wireOp",EDGE,"E23");var subQ3=sQuery(id+"F0.wireOp",EDGE,"E0.bottom");var subQ4=makeQuery(id+"F1.opExtrude","CAP_EDGE",EDGE,{"disambiguationData":[OSD([subQ3])],"isStart":true});var subQ5=sQuery(id+"F0.wireOp",EDGE,"E0.right");var subQ6=makeQuery(id+"F3.imprint","INTERSECT",VERTEX,{"derivedFrom":[makeQuery(id+"F1.opExtrude","SWEPT_EDGE",EDGE,{"disambiguationData":[OSD([subQ3,subQ5])]}),subQ4]});var subQ7=makeQuery(id+"F4.boolean.opBoolean","MERGE",EDGE,{"derivedFrom":[makeQuery(id+"F1.opExtrude","CAP_EDGE",EDGE,{"disambiguationData":[OSD([subQ5])],"isStart":true}),makeQuery(id+"F4.opExtrude","SWEPT_EDGE",EDGE,{"disambiguationData":[OSD([subQ3,subQ5]),TDD([subQ6])]})]});var subQ14=subQ7;var subQ15=makeQuery(id+"F13.imprint","IMPRINT",EDGE,{"disambiguationData":[TD([[makeQuery(id+"F13.imprint","INTERSECT",VERTEX,{"derivedFrom":[subQ14,subQ2]}),1.0]])],"derivedFrom":subQ14});Q14=makeQuery(id+"F22.boolean.opBoolean","SPLIT",EDGE,{"disambiguationData":[TD([makeQuery(id+"F14.opExtrude","SWEPT_FACE",FACE,{"disambiguationData":[OSD([subQ2])]})])],"derivedFrom":makeQuery(id+"F14.opExtrude","CAP_EDGE",EDGE,{"disambiguationData":[OSD([subQ3,subQ5]),TDD([subQ15])],"isStart":false})});}
            var Q15;
            {var subQ0=sQuery(id+"F13.wireOp",EDGE,"E24");var subQ1=sQuery(id+"F13.wireOp",EDGE,"E23");var subQ2=sQuery(id+"F0.wireOp",EDGE,"E0.right");var subQ3=sQuery(id+"F0.wireOp",EDGE,"E0.bottom");var subQ6=makeQuery(id+"F1.opExtrude","CAP_EDGE",EDGE,{"disambiguationData":[OSD([subQ3])],"isStart":true});var subQ7=makeQuery(id+"F3.imprint","INTERSECT",VERTEX,{"derivedFrom":[makeQuery(id+"F1.opExtrude","SWEPT_EDGE",EDGE,{"disambiguationData":[OSD([subQ3,subQ2])]}),subQ6]});var subQ8=makeQuery(id+"F4.boolean.opBoolean","MERGE",EDGE,{"derivedFrom":[makeQuery(id+"F1.opExtrude","CAP_EDGE",EDGE,{"disambiguationData":[OSD([subQ2])],"isStart":true}),makeQuery(id+"F4.opExtrude","SWEPT_EDGE",EDGE,{"disambiguationData":[OSD([subQ3,subQ2]),TDD([subQ7])]})]});var subQ14=subQ8;var subQ15=makeQuery(id+"F13.imprint","IMPRINT",EDGE,{"disambiguationData":[TD([[makeQuery(id+"F13.imprint","INTERSECT",VERTEX,{"derivedFrom":[subQ14,subQ1]}),1.0]])],"derivedFrom":subQ14});Q15=makeQuery(id+"F22.boolean.opBoolean","SPLIT",EDGE,{"disambiguationData":[TD([makeQuery(id+"F14.opExtrude","SWEPT_FACE",FACE,{"disambiguationData":[OSD([subQ0])]})])],"derivedFrom":makeQuery(id+"F14.opExtrude","CAP_EDGE",EDGE,{"disambiguationData":[OSD([subQ3,subQ2]),TDD([subQ15])],"isStart":false})});}
            var Q16;
            Q16=makeQuery(id+"F14.opExtrude","CAP_EDGE",EDGE,{"disambiguationData":[OSD([sQuery(id+"F13.wireOp",EDGE,"E23")])],"isStart":true});
            var Q17;
            Q17=makeQuery(id+"F14.opExtrude","CAP_EDGE",EDGE,{"disambiguationData":[OSD([sQuery(id+"F13.wireOp",EDGE,"E24")])],"isStart":true});
            var Q18;
            Q18=makeQuery(id+"F18.opExtrude","CAP_EDGE",EDGE,{"disambiguationData":[OSD([sQuery(id+"F17.wireOp",EDGE,"E33")])],"isStart":true});
            var Q19;
            Q19=makeQuery(id+"F18.opExtrude","CAP_EDGE",EDGE,{"disambiguationData":[OSD([sQuery(id+"F17.wireOp",EDGE,"E32")])],"isStart":true});
            fillet(context, id + "F23", {"entities" : qUnion([Q0, Q1, Q2, Q3, Q4, Q5, Q6, Q7, Q8, Q9, Q10, Q11, Q12, Q13, Q14, Q15, Q16, Q17, Q18, Q19]), "radius" : 2 * mm, "tangentPropagation" : true, "allowEdgeOverflow" : false});
        }
    });
